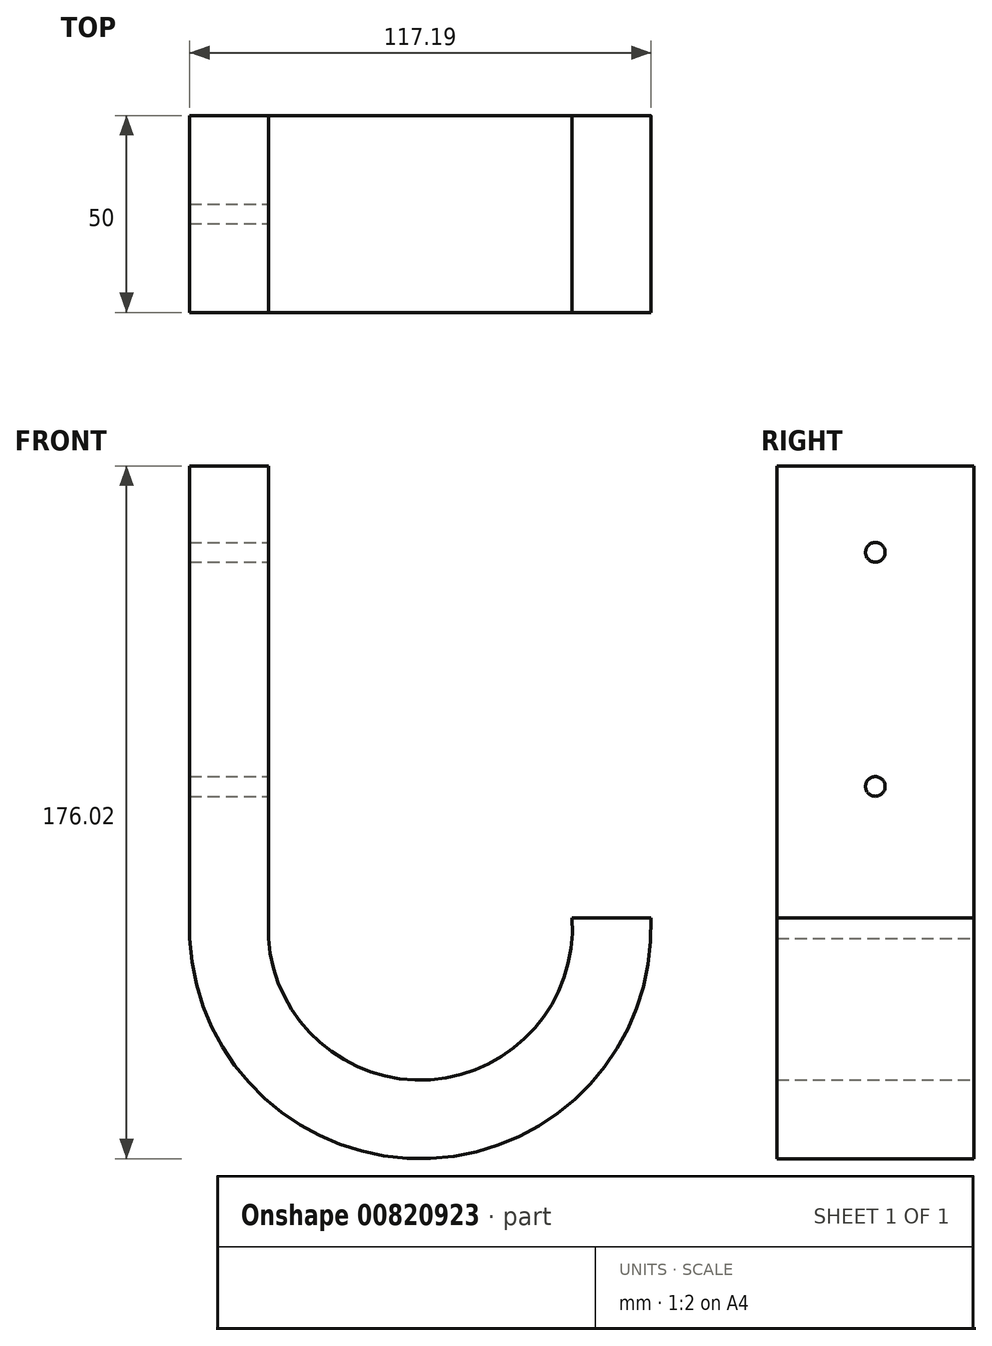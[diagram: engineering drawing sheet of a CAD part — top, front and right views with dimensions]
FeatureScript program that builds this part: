
annotation { "Feature Type Name" : "Feature", "Feature Type Description" : "" }
export const myFeature = defineFeature(function(context is Context, id is Id, definition is map)
    precondition{}
    {
        {
            var Q0;
            Q0=qCreatedBy(makeId("Front.planeOp"),FACE);
            var sketch = newSketch(context, id + "F0", { "sketchPlane" : qUnion([Q0])});
            skLineSegment(sketch, "E0.bottom", {"start": v(10, 60) * mm, "end": v(-10, 60) * mm});
            skLineSegment(sketch, "E0.top", {"start": v(10, -60) * mm, "end": v(-10, -60) * mm});
            skLineSegment(sketch, "E0.left", {"start": v(10, 60) * mm, "end": v(10, -60) * mm});
            skLineSegment(sketch, "E0.right", {"start": v(-10, 60) * mm, "end": v(-10, -60) * mm});
            skPoint(sketch, "E0.middle", {"position": v(0, 0) * mm});
            skArc(sketch, "E1", {"start": v(10, -60) * mm, "mid": v(51.17, -95.96) * mm, "end": v(87.13, -54.8) * mm});
            skArc(sketch, "E2", {"start": v(-10, -60) * mm, "mid": v(52.81, -115.87) * mm, "end": v(106.89, -51.5) * mm});
            skLineSegment(sketch, "E3", {"start": v(87.13, -54.8) * mm, "end": v(107.13, -54.8) * mm});
            skSolve(sketch);
        }
        {
            var Q0;
            Q0=makeQuery(id+"F0.imprint","IMPRINT",FACE,{"disambiguationData":[TD([[makeQuery(id+"F0.imprint","IMPRINT",EDGE,{"derivedFrom":sQuery(id+"F0.wireOp",EDGE,"E0.bottom")}),1.0]])]});
            var Q1;
            {var subQ0=sQuery(id+"F0.wireOp",EDGE,"E0.top");Q1=makeQuery(id+"F0.imprint","IMPRINT",FACE,{"disambiguationData":[TD([[makeQuery(id+"F0.imprint","IMPRINT",EDGE,{"derivedFrom":subQ0}),1.0]])]});}
            extrude(context, id + "F1", {"entities" : qUnion([Q0, Q1]), "endBound" : BoundingType.SYMMETRIC, "depth" : 50 * mm, "offsetDistance" : 25 * mm});
        }
        {
            var Q0;
            Q0=makeQuery(id+"F1.opExtrude","SWEPT_FACE",FACE,{"disambiguationData":[OSD([sQuery(id+"F0.wireOp",EDGE,"E0.left")])]});
            var sketch = newSketch(context, id + "F2", { "sketchPlane" : qUnion([Q0])});
            skCircle(sketch, "E4", {"center": v(0, 38.04) * mm, "radius": 2.5 * mm});
            skCircle(sketch, "E5", {"center": v(0, -21.44) * mm, "radius": 2.5 * mm});
            skSolve(sketch);
        }
        {
            var Q0;
            Q0=makeQuery(id+"F2.imprint","IMPRINT",FACE,{"disambiguationData":[TD([[makeQuery(id+"F2.imprint","IMPRINT",EDGE,{"derivedFrom":sQuery(id+"F2.wireOp",EDGE,"E5")}),1.0]])]});
            var Q1;
            Q1=makeQuery(id+"F2.imprint","IMPRINT",FACE,{"disambiguationData":[TD([[makeQuery(id+"F2.imprint","IMPRINT",EDGE,{"derivedFrom":sQuery(id+"F2.wireOp",EDGE,"E4")}),1.0]])]});
            var Q2;
            Q2=sQuery(id+"F2.wireOp",EDGE,"E4");
            var Q3;
            Q3=sQuery(id+"F2.wireOp",EDGE,"E5");
            extrude(context, id + "F3", {"entities" : qUnion([Q0, Q1]), "operationType" : NewBodyOperationType.REMOVE, "surfaceEntities" : qUnion([Q2, Q3]), "endBound" : BoundingType.THROUGH_ALL, "oppositeDirection" : true, "depth" : 25 * mm, "offsetDistance" : 25 * mm});
        }
    });
